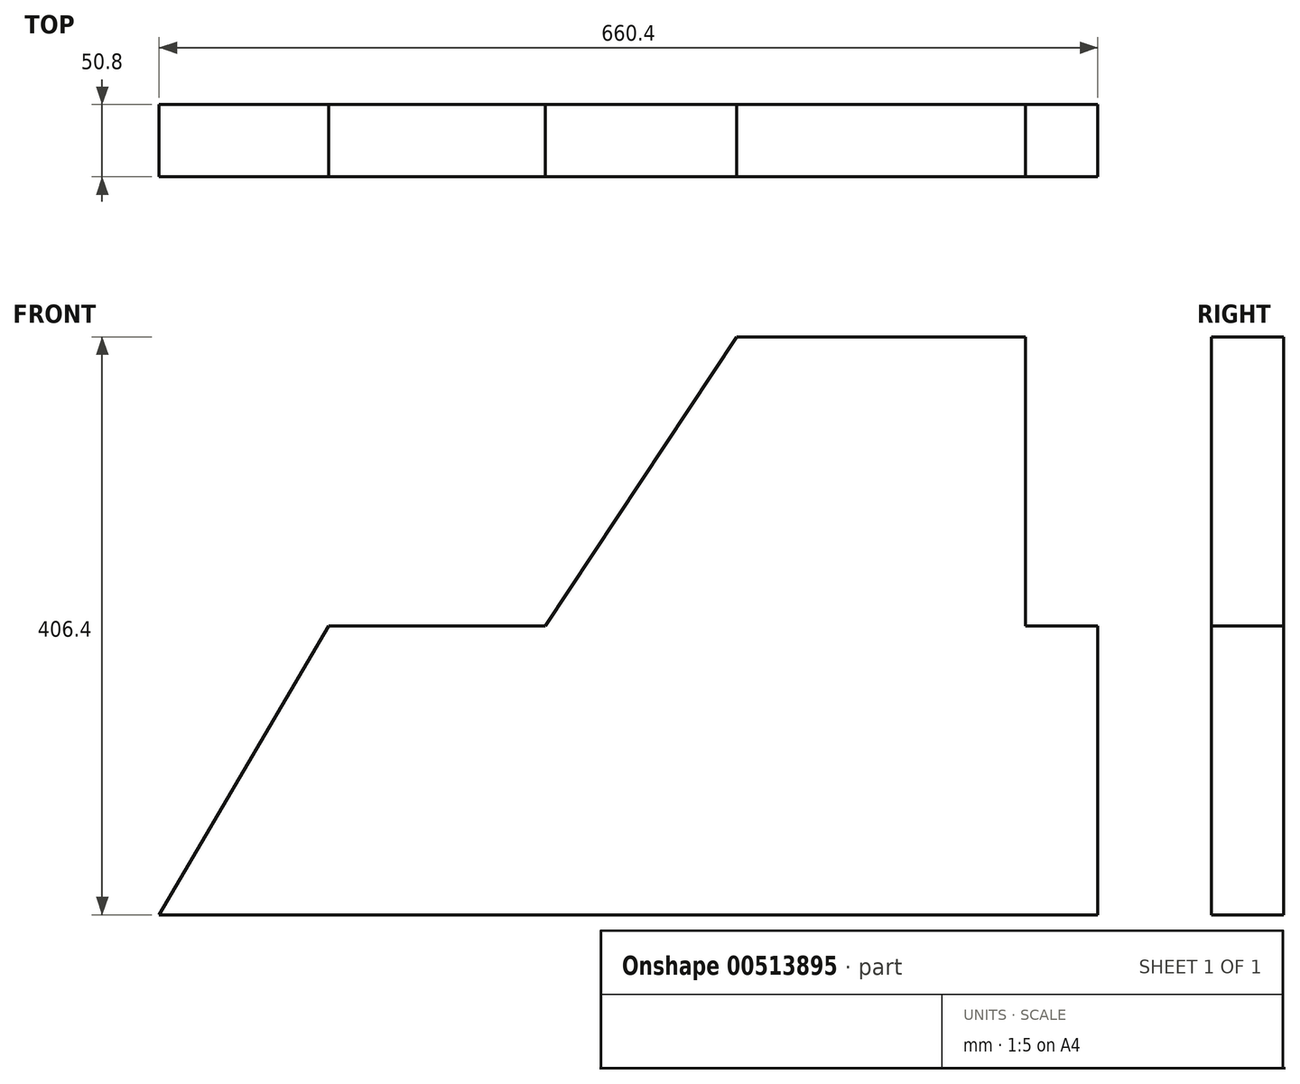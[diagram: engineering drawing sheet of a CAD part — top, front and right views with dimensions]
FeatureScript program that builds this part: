
annotation { "Feature Type Name" : "Feature", "Feature Type Description" : "" }
export const myFeature = defineFeature(function(context is Context, id is Id, definition is map)
    precondition{}
    {
        {
            var Q0;
            Q0=qCreatedBy(makeId("Front.planeOp"),FACE);
            var sketch = newSketch(context, id + "F0", { "sketchPlane" : qUnion([Q0])});
            skLineSegment(sketch, "E0", {"start": v(0, 0) * mm, "end": v(660.4, 0) * mm});
            skLineSegment(sketch, "E1", {"start": v(660.4, 0) * mm, "end": v(660.4, 203.2) * mm});
            skLineSegment(sketch, "E2", {"start": v(660.4, 203.2) * mm, "end": v(609.6, 203.2) * mm});
            skLineSegment(sketch, "E3", {"start": v(609.6, 203.2) * mm, "end": v(609.6, 406.4) * mm});
            skLineSegment(sketch, "E4", {"start": v(609.6, 406.4) * mm, "end": v(406.4, 406.4) * mm});
            skLineSegment(sketch, "E5", {"start": v(406.4, 406.4) * mm, "end": v(271.75, 203.2) * mm});
            skLineSegment(sketch, "E6", {"start": v(271.75, 203.2) * mm, "end": v(119.35, 203.2) * mm});
            skLineSegment(sketch, "E7", {"start": v(119.35, 203.2) * mm, "end": v(0, 0) * mm});
            skSolve(sketch);
        }
        {
            var Q0;
            Q0=makeQuery(id+"F0.imprint","IMPRINT",FACE,{"disambiguationData":[TD([[makeQuery(id+"F0.imprint","IMPRINT",EDGE,{"derivedFrom":sQuery(id+"F0.wireOp",EDGE,"E0")}),1.0]])]});
            extrude(context, id + "F1", {"entities" : qUnion([Q0]), "depth" : 50.8 * mm, "offsetDistance" : 25.4 * mm});
        }
    });
